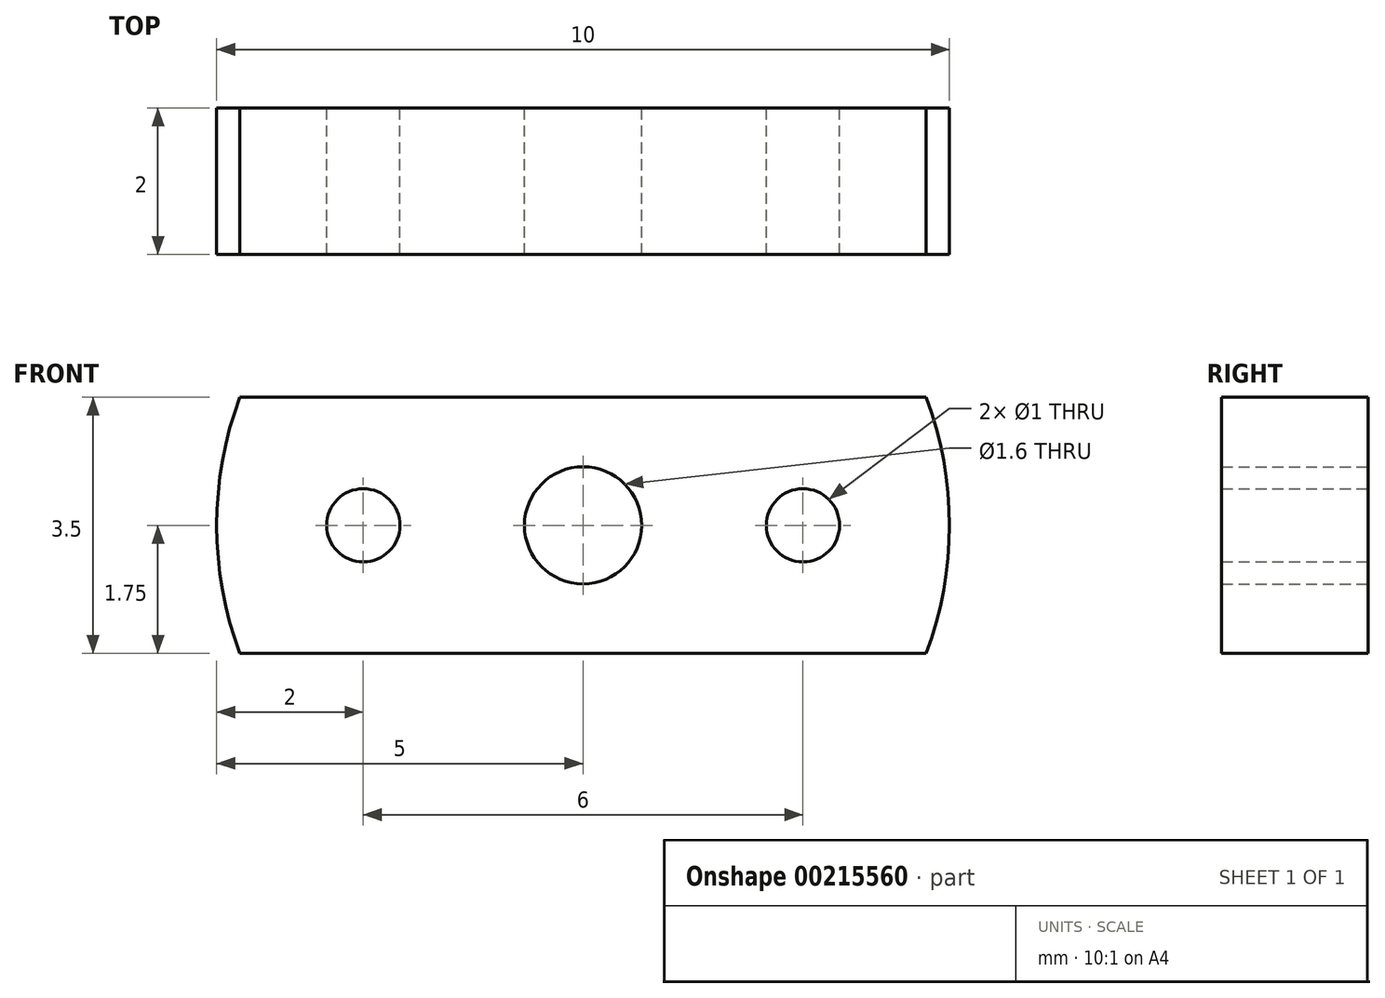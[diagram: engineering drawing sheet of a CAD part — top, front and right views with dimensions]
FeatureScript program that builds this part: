
annotation { "Feature Type Name" : "Feature", "Feature Type Description" : "" }
export const myFeature = defineFeature(function(context is Context, id is Id, definition is map)
    precondition{}
    {
        {
            var Q0;
            Q0=qCreatedBy(makeId("Front.planeOp"),FACE);
            var sketch = newSketch(context, id + "F0", { "sketchPlane" : qUnion([Q0])});
            skArc(sketch, "E0", {"start": v(-4.68, 1.75) * mm, "mid": v(-5, 0) * mm, "end": v(-4.68, -1.75) * mm});
            skCircle(sketch, "E1", {"center": v(0, 0) * mm, "radius": 0.8 * mm});
            skCircle(sketch, "E2", {"center": v(-3, 0) * mm, "radius": 0.5 * mm});
            skCircle(sketch, "E3", {"center": v(3, 0) * mm, "radius": 0.5 * mm});
            skLineSegment(sketch, "E4.bottom", {"start": v(-4.68, 1.75) * mm, "end": v(4.68, 1.75) * mm});
            skLineSegment(sketch, "E4.top", {"start": v(-4.68, -1.75) * mm, "end": v(4.68, -1.75) * mm});
            skLineSegment(sketch, "E5", {"start": v(0, 1.75) * mm, "end": v(0, 0) * mm, "construction": true});
            skLineSegment(sketch, "E6", {"start": v(0, 0) * mm, "end": v(7.9, 0) * mm, "construction": true});
            skArc(sketch, "E7.trimOffspring", {"start": v(4.68, -1.75) * mm, "mid": v(5, 0) * mm, "end": v(4.68, 1.75) * mm});
            skPoint(sketch, "E8.orphan", {"position": v(-7.9, 1.75) * mm});
            skPoint(sketch, "E9.orphan", {"position": v(7.9, 1.75) * mm});
            skPoint(sketch, "E10.orphan", {"position": v(7.9, -1.75) * mm});
            skSolve(sketch);
        }
        {
            var Q0;
            Q0 = qSketchRegion(id + "F0", true);
            extrude(context, id + "F1", {"entities" : qUnion([Q0]), "depth" : 2 * mm});
        }
    });
